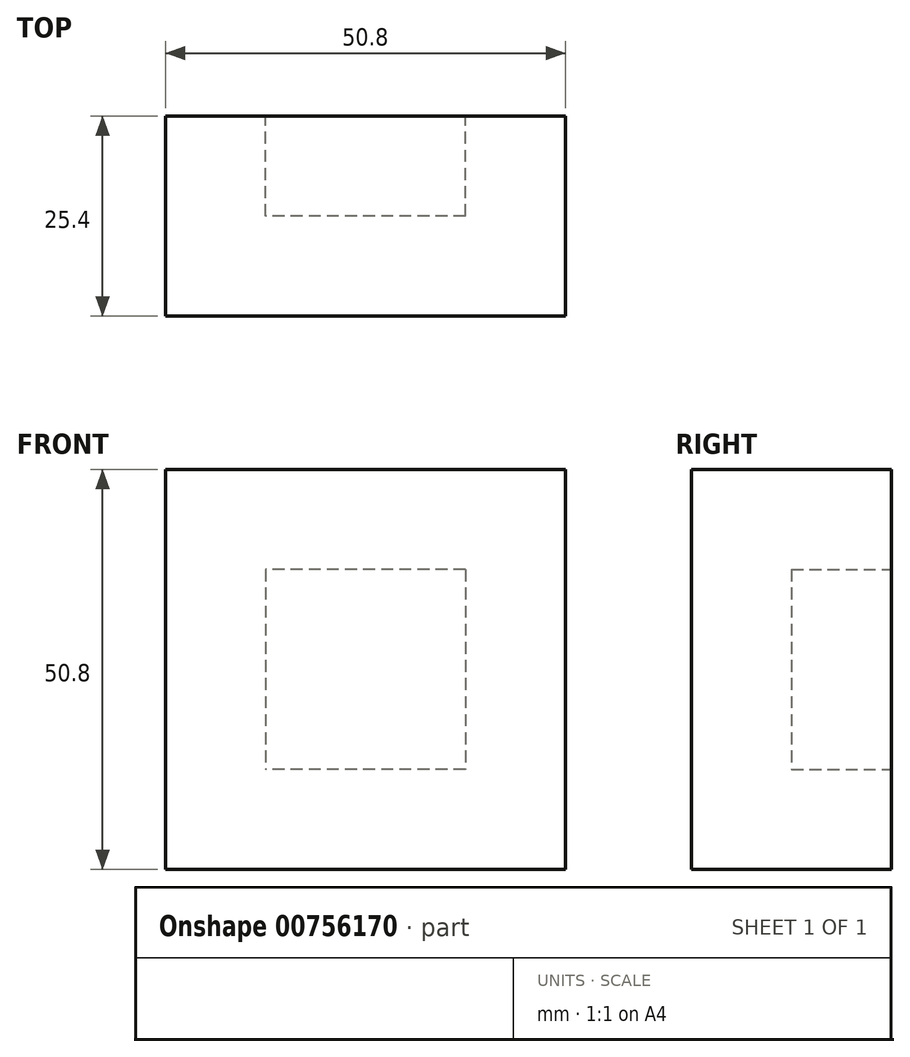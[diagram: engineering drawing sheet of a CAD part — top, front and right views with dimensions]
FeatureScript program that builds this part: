
annotation { "Feature Type Name" : "Feature", "Feature Type Description" : "" }
export const myFeature = defineFeature(function(context is Context, id is Id, definition is map)
    precondition{}
    {
        {
            var Q0;
            Q0=qCreatedBy(makeId("Front.planeOp"),FACE);
            var sketch = newSketch(context, id + "F0", { "sketchPlane" : qUnion([Q0])});
            skLineSegment(sketch, "E0.bottom", {"start": v(25.4, 25.4) * mm, "end": v(-25.4, 25.4) * mm});
            skLineSegment(sketch, "E0.top", {"start": v(25.4, -25.4) * mm, "end": v(-25.4, -25.4) * mm});
            skLineSegment(sketch, "E0.left", {"start": v(25.4, 25.4) * mm, "end": v(25.4, -25.4) * mm});
            skLineSegment(sketch, "E0.right", {"start": v(-25.4, 25.4) * mm, "end": v(-25.4, -25.4) * mm});
            skPoint(sketch, "E0.middle", {"position": v(0, 0) * mm});
            skSolve(sketch);
        }
        {
            var Q0;
            Q0=makeQuery(id+"F0.imprint","IMPRINT",FACE,{"disambiguationData":[TD([[makeQuery(id+"F0.imprint","IMPRINT",EDGE,{"derivedFrom":sQuery(id+"F0.wireOp",EDGE,"E0.bottom")}),1.0]])]});
            extrude(context, id + "F1", {"entities" : qUnion([Q0]), "depth" : 25.4 * mm, "offsetDistance" : 25.4 * mm});
        }
        {
            var Q0;
            Q0=makeQuery(id+"F1.opExtrude","CAP_FACE",FACE,{"disambiguationData":[OSD([sQuery(id+"F0.wireOp",EDGE,"E0.bottom"),sQuery(id+"F0.wireOp",EDGE,"E0.top"),sQuery(id+"F0.wireOp",EDGE,"E0.left"),sQuery(id+"F0.wireOp",EDGE,"E0.right")])],"isStart":true});
            shell(context, id + "F2", {"entities" : qUnion([Q0]), "thickness" : 12.7 * mm});
        }
    });
